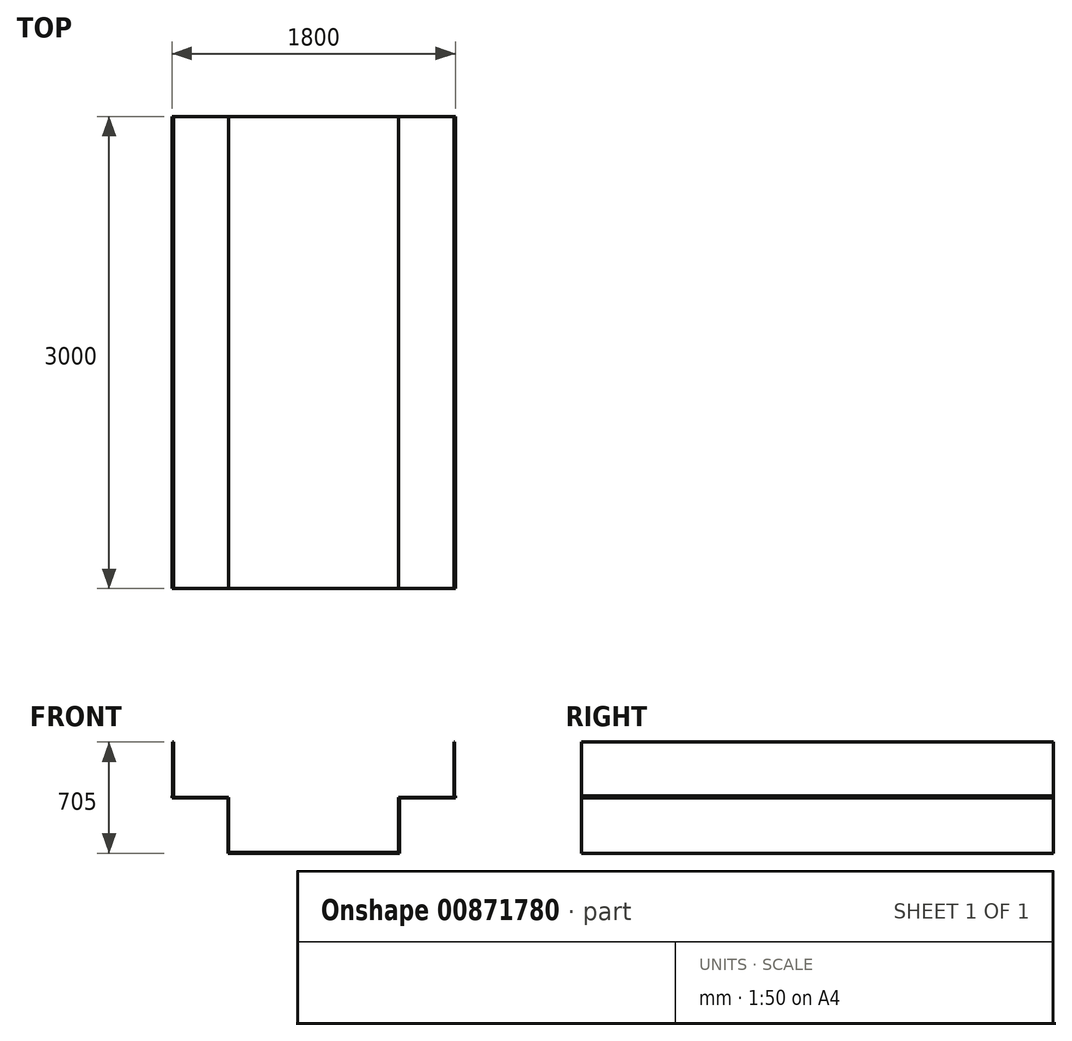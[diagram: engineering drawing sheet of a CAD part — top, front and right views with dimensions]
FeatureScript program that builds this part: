
annotation { "Feature Type Name" : "Feature", "Feature Type Description" : "" }
export const myFeature = defineFeature(function(context is Context, id is Id, definition is map)
    precondition{}
    {
        {
            var Q0;
            Q0=qCreatedBy(makeId("Front.planeOp"),FACE);
            var sketch = newSketch(context, id + "F0", { "sketchPlane" : qUnion([Q0])});
            skLineSegment(sketch, "E0", {"start": v(0, 923.44) * mm, "end": v(0, -700) * mm, "construction": true});
            skLineSegment(sketch, "E1", {"start": v(0, -700) * mm, "end": v(-540, -700) * mm});
            skLineSegment(sketch, "E2", {"start": v(-540, -700) * mm, "end": v(-540, -350) * mm});
            skLineSegment(sketch, "E3", {"start": v(-540, -350) * mm, "end": v(-890, -350) * mm});
            skLineSegment(sketch, "E4", {"start": v(-895, -340) * mm, "end": v(-895, 0) * mm});
            skLineSegment(sketch, "E5.0", {"start": v(-900, -355) * mm, "end": v(-900, -340) * mm});
            skLineSegment(sketch, "E5.1", {"start": v(-545, -355) * mm, "end": v(-900, -355) * mm});
            skLineSegment(sketch, "E5.2", {"start": v(-545, -705) * mm, "end": v(-545, -355) * mm});
            skLineSegment(sketch, "E5.3", {"start": v(0, -705) * mm, "end": v(-545, -705) * mm});
            skLineSegment(sketch, "E6.MirrorCS", {"start": v(0, -705) * mm, "end": v(545, -705) * mm});
            skLineSegment(sketch, "E7.MirrorCS", {"start": v(0, -700) * mm, "end": v(540, -700) * mm});
            skLineSegment(sketch, "E8.MirrorCS", {"start": v(540, -700) * mm, "end": v(540, -350) * mm});
            skLineSegment(sketch, "E9.MirrorCS", {"start": v(545, -705) * mm, "end": v(545, -355) * mm});
            skLineSegment(sketch, "E10.MirrorCS", {"start": v(545, -355) * mm, "end": v(900, -355) * mm});
            skLineSegment(sketch, "E11.MirrorCS", {"start": v(540, -350) * mm, "end": v(895, -350) * mm});
            skPoint(sketch, "E12.MirrorCS.end.orphan", {"position": v(0, -700) * mm});
            skPoint(sketch, "E12.MirrorCS.start.orphan", {"position": v(0, -705) * mm});
            skLineSegment(sketch, "E13.trimOffspring", {"start": v(0, -705) * mm, "end": v(0, -930.47) * mm, "construction": true});
            skLineSegment(sketch, "E14.0", {"start": v(-890, -350) * mm, "end": v(-890, 0) * mm});
            skLineSegment(sketch, "E15", {"start": v(-895, 0) * mm, "end": v(-890, 0) * mm});
            skLineSegment(sketch, "E16", {"start": v(-900, -340) * mm, "end": v(-895, -340) * mm});
            skPoint(sketch, "E17.orphan", {"position": v(-895, -350) * mm});
            skPoint(sketch, "E18.MirrorCS.end.orphan", {"position": v(900, -340) * mm});
            skPoint(sketch, "E18.MirrorCS.start.orphan", {"position": v(895, 0) * mm});
            skPoint(sketch, "E19.MirrorCS.start.orphan", {"position": v(895, -350) * mm});
            skPoint(sketch, "E20.MirrorCS.start.orphan", {"position": v(900, -355) * mm});
            skLineSegment(sketch, "E21.MirrorCS", {"start": v(890, -350) * mm, "end": v(890, 0) * mm});
            skLineSegment(sketch, "E22.MirrorCS", {"start": v(900, -355) * mm, "end": v(900, -340) * mm});
            skLineSegment(sketch, "E23.MirrorCS", {"start": v(900, -340) * mm, "end": v(895, -340) * mm});
            skLineSegment(sketch, "E24.MirrorCS", {"start": v(895, -340) * mm, "end": v(895, 0) * mm});
            skLineSegment(sketch, "E25.MirrorCS", {"start": v(895, 0) * mm, "end": v(890, 0) * mm});
            skSolve(sketch);
        }
        {
            var Q0;
            Q0=makeQuery(id+"F0.imprint","IMPRINT",FACE,{"disambiguationData":[TD([[makeQuery(id+"F0.imprint","IMPRINT",EDGE,{"derivedFrom":sQuery(id+"F0.wireOp",EDGE,"E1")}),1.0]])]});
            extrude(context, id + "F1", {"entities" : qUnion([Q0]), "depth" : 1500 * mm, "offsetDistance" : 25 * mm, "hasSecondDirection" : true, "secondDirectionOppositeDirection" : true, "secondDirectionDepth" : 1500 * mm});
        }
    });
